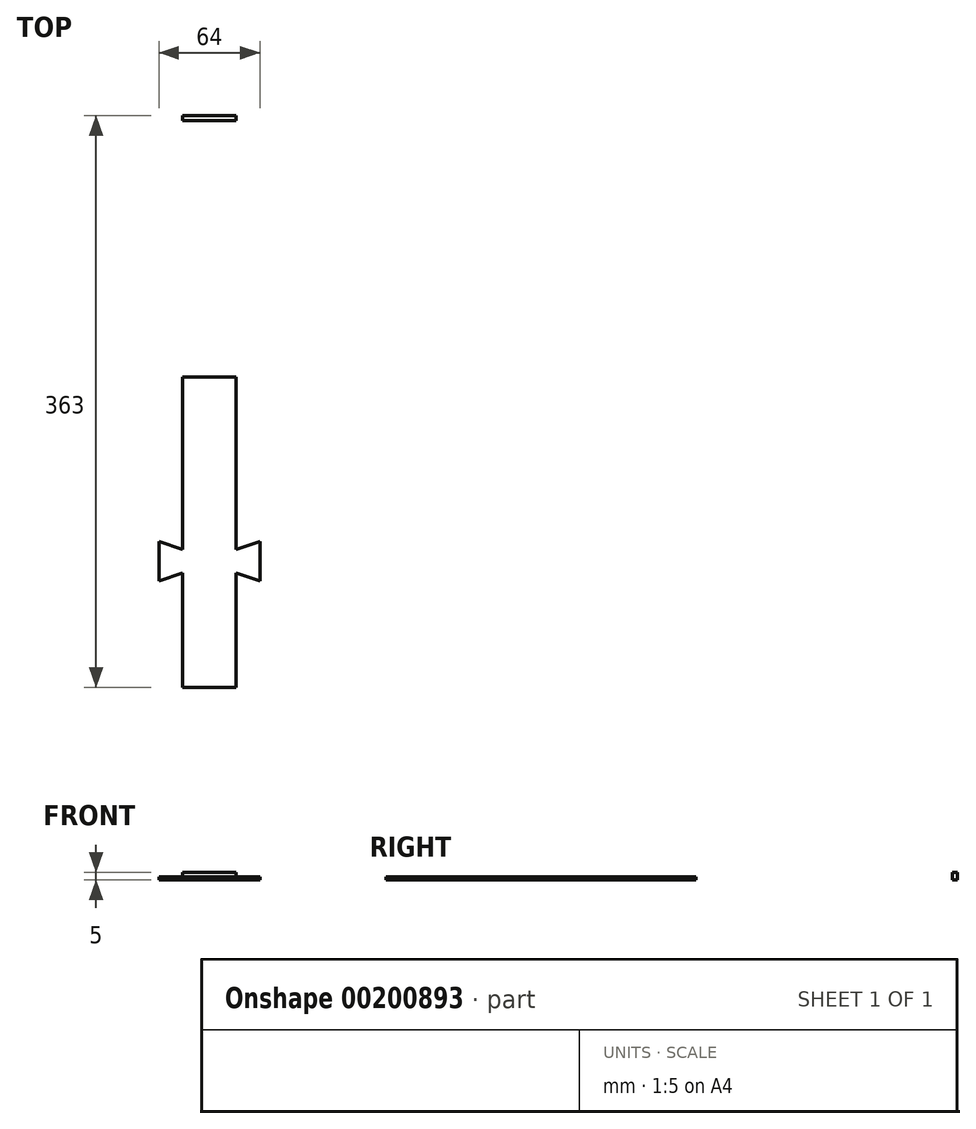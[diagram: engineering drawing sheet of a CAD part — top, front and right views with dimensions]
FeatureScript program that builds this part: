
annotation { "Feature Type Name" : "Feature", "Feature Type Description" : "" }
export const myFeature = defineFeature(function(context is Context, id is Id, definition is map)
    precondition{}
    {
        {
            var Q0;
            Q0=qCreatedBy(makeId("Top.planeOp"),FACE);
            var sketch = newSketch(context, id + "F0", { "sketchPlane" : qUnion([Q0])});
            skLineSegment(sketch, "E0.bottom", {"start": v(180, 180) * mm, "end": v(-180, 180) * mm});
            skLineSegment(sketch, "E0.top", {"start": v(180, -180) * mm, "end": v(-180, -180) * mm});
            skLineSegment(sketch, "E0.left", {"start": v(180, 180) * mm, "end": v(180, -180) * mm});
            skLineSegment(sketch, "E0.right", {"start": v(-180, 180) * mm, "end": v(-180, -180) * mm});
            skPoint(sketch, "E0.middle", {"position": v(0, 0) * mm});
            skLineSegment(sketch, "E1.bottom", {"start": v(183, 183) * mm, "end": v(-183, 183) * mm});
            skLineSegment(sketch, "E1.top", {"start": v(183, -183) * mm, "end": v(-183, -183) * mm});
            skLineSegment(sketch, "E1.left", {"start": v(183, 183) * mm, "end": v(183, -183) * mm});
            skLineSegment(sketch, "E1.right", {"start": v(-183, 183) * mm, "end": v(-183, -183) * mm});
            skSolve(sketch);
        }
        {
            var Q0;
            Q0=makeQuery(id+"F0.imprint","IMPRINT",FACE,{"disambiguationData":[TD([[makeQuery(id+"F0.imprint","IMPRINT",EDGE,{"derivedFrom":sQuery(id+"F0.wireOp",EDGE,"E0.bottom")}),1.0]])]});
            extrude(context, id + "F1", {"entities" : qUnion([Q0]), "depth" : 2 * mm});
        }
        {
            var Q0;
            Q0=makeQuery(id+"F0.imprint","IMPRINT",FACE,{"disambiguationData":[TD([[makeQuery(id+"F0.imprint","IMPRINT",EDGE,{"derivedFrom":sQuery(id+"F0.wireOp",EDGE,"E0.bottom")}),-1.0]])]});
            extrude(context, id + "F2", {"entities" : qUnion([Q0]), "operationType" : NewBodyOperationType.ADD, "depth" : 5 * mm});
        }
        {
            var Q0;
            Q0=makeQuery(id+"F2.opExtrude","CAP_FACE",FACE,{"disambiguationData":[OSD([sQuery(id+"F0.wireOp",EDGE,"E0.bottom"),sQuery(id+"F0.wireOp",EDGE,"E0.top"),sQuery(id+"F0.wireOp",EDGE,"E0.left"),sQuery(id+"F0.wireOp",EDGE,"E0.right"),sQuery(id+"F0.wireOp",EDGE,"E1.bottom"),sQuery(id+"F0.wireOp",EDGE,"E1.top"),sQuery(id+"F0.wireOp",EDGE,"E1.left"),sQuery(id+"F0.wireOp",EDGE,"E1.right")])],"isStart":false});
            var sketch = newSketch(context, id + "F3", { "sketchPlane" : qUnion([Q0])});
            skLineSegment(sketch, "E2", {"start": v(0, 0) * mm, "end": v(0, 194.54) * mm, "construction": true});
            skPoint(sketch, "E2.endSnap0", {"position": v(0, 183) * mm});
            skLineSegment(sketch, "E3", {"start": v(0, 194.54) * mm, "end": v(0, 0) * mm, "construction": true});
            skLineSegment(sketch, "E4", {"start": v(220.84, 0) * mm, "end": v(0, 0) * mm, "construction": true});
            skLineSegment(sketch, "E5.bottom", {"start": v(17, -17) * mm, "end": v(-92.5, -17) * mm});
            skLineSegment(sketch, "E5.top", {"start": v(17, 183) * mm, "end": v(-183, 183) * mm});
            skLineSegment(sketch, "E5.left", {"start": v(17, -17) * mm, "end": v(17, 92.5) * mm});
            skLineSegment(sketch, "E5.right", {"start": v(-183, -17) * mm, "end": v(-183, 183) * mm});
            skPoint(sketch, "E5.middle", {"position": v(-83, 83) * mm});
            skLineSegment(sketch, "E6.MirrorCS", {"start": v(-17, -17) * mm, "end": v(-17, 92.5) * mm});
            skLineSegment(sketch, "E7.MirrorCS", {"start": v(17, 17) * mm, "end": v(-92.5, 17) * mm});
            skLineSegment(sketch, "E8", {"start": v(-17, 17) * mm, "end": v(-17, 92.5) * mm, "construction": true});
            skLineSegment(sketch, "E9", {"start": v(-17, 100) * mm, "end": v(-183, 100) * mm, "construction": true});
            skLineSegment(sketch, "E10", {"start": v(-100, 17) * mm, "end": v(-100, 183) * mm, "construction": true});
            skLineSegment(sketch, "E11", {"start": v(-32, 87.5) * mm, "end": v(-32, 112.5) * mm});
            skLineSegment(sketch, "E12", {"start": v(-17, 92.5) * mm, "end": v(-32, 87.5) * mm});
            skLineSegment(sketch, "E13.MirrorCS", {"start": v(-17, 107.5) * mm, "end": v(-32, 112.5) * mm});
            skLineSegment(sketch, "E14.MirrorCS", {"start": v(17, 92.5) * mm, "end": v(32, 87.5) * mm});
            skLineSegment(sketch, "E15.MirrorCS", {"start": v(32, 87.5) * mm, "end": v(32, 112.5) * mm});
            skLineSegment(sketch, "E16.MirrorCS", {"start": v(17, 107.5) * mm, "end": v(32, 112.5) * mm});
            skLineSegment(sketch, "E17.trimOffspring", {"start": v(17, 107.5) * mm, "end": v(17, 183) * mm});
            skLineSegment(sketch, "E18.trimOffspring", {"start": v(-17, 107.5) * mm, "end": v(-17, 183) * mm, "construction": true});
            skLineSegment(sketch, "E19.trimOffspring", {"start": v(-17, 107.5) * mm, "end": v(-17, 183) * mm});
            skLineSegment(sketch, "E20.1.0", {"start": v(17, 17) * mm, "end": v(92.5, 17) * mm, "construction": true});
            skLineSegment(sketch, "E20.1.2", {"start": v(17, 17) * mm, "end": v(17, 92.5) * mm, "construction": true});
            skLineSegment(sketch, "E20.1.5", {"start": v(107.5, 17) * mm, "end": v(112.5, 32) * mm});
            skPoint(sketch, "E20.1.6", {"position": v(83, 83) * mm});
            skLineSegment(sketch, "E20.1.7", {"start": v(-17, 17) * mm, "end": v(92.5, 17) * mm});
            skLineSegment(sketch, "E20.1.8", {"start": v(107.5, -17) * mm, "end": v(112.5, -32) * mm});
            skLineSegment(sketch, "E20.1.9", {"start": v(92.5, -17) * mm, "end": v(87.5, -32) * mm});
            skLineSegment(sketch, "E20.1.10", {"start": v(87.5, -32) * mm, "end": v(112.5, -32) * mm});
            skLineSegment(sketch, "E20.1.11", {"start": v(107.5, 17) * mm, "end": v(183, 17) * mm, "construction": true});
            skLineSegment(sketch, "E20.1.12", {"start": v(92.5, 17) * mm, "end": v(87.5, 32) * mm});
            skLineSegment(sketch, "E20.1.13", {"start": v(-17, -17) * mm, "end": v(92.5, -17) * mm});
            skLineSegment(sketch, "E20.1.14", {"start": v(87.5, 32) * mm, "end": v(112.5, 32) * mm});
            skLineSegment(sketch, "E20.1.16", {"start": v(107.5, -17) * mm, "end": v(183, -17) * mm});
            skLineSegment(sketch, "E20.1.18", {"start": v(107.5, 17) * mm, "end": v(183, 17) * mm});
            skLineSegment(sketch, "E20.2.0", {"start": v(17, -17) * mm, "end": v(17, -92.5) * mm, "construction": true});
            skLineSegment(sketch, "E20.2.5", {"start": v(17, -107.5) * mm, "end": v(32, -112.5) * mm});
            skPoint(sketch, "E20.2.6", {"position": v(83, -83) * mm});
            skLineSegment(sketch, "E20.2.7", {"start": v(17, 17) * mm, "end": v(17, -92.5) * mm});
            skLineSegment(sketch, "E20.2.8", {"start": v(-17, -107.5) * mm, "end": v(-32, -112.5) * mm});
            skLineSegment(sketch, "E20.2.9", {"start": v(-17, -92.5) * mm, "end": v(-32, -87.5) * mm});
            skLineSegment(sketch, "E20.2.10", {"start": v(-32, -87.5) * mm, "end": v(-32, -112.5) * mm});
            skLineSegment(sketch, "E20.2.11", {"start": v(17, -107.5) * mm, "end": v(17, -183) * mm, "construction": true});
            skLineSegment(sketch, "E20.2.12", {"start": v(17, -92.5) * mm, "end": v(32, -87.5) * mm});
            skLineSegment(sketch, "E20.2.13", {"start": v(-17, 17) * mm, "end": v(-17, -92.5) * mm});
            skLineSegment(sketch, "E20.2.14", {"start": v(32, -87.5) * mm, "end": v(32, -112.5) * mm});
            skLineSegment(sketch, "E20.2.15", {"start": v(-17, -17) * mm, "end": v(92.5, -17) * mm});
            skLineSegment(sketch, "E20.2.16", {"start": v(-17, -107.5) * mm, "end": v(-17, -183) * mm});
            skLineSegment(sketch, "E20.2.18", {"start": v(17, -107.5) * mm, "end": v(17, -183) * mm});
            skPoint(sketch, "E20.center", {"position": v(0, 0) * mm});
            skLineSegment(sketch, "E21.trimOffspring", {"start": v(107.5, -17) * mm, "end": v(183, -17) * mm, "construction": true});
            skLineSegment(sketch, "E22.trimOffspring", {"start": v(17, 107.5) * mm, "end": v(17, 183) * mm, "construction": true});
            skLineSegment(sketch, "E23.MirrorCS", {"start": v(-107.5, 17) * mm, "end": v(-112.5, 32) * mm});
            skLineSegment(sketch, "E24.MirrorCS", {"start": v(-87.5, 32) * mm, "end": v(-112.5, 32) * mm});
            skLineSegment(sketch, "E25.MirrorCS", {"start": v(-92.5, 17) * mm, "end": v(-87.5, 32) * mm});
            skLineSegment(sketch, "E26.MirrorCS", {"start": v(-92.5, -17) * mm, "end": v(-87.5, -32) * mm});
            skLineSegment(sketch, "E27.MirrorCS", {"start": v(-87.5, -32) * mm, "end": v(-112.5, -32) * mm});
            skLineSegment(sketch, "E28.MirrorCS", {"start": v(-107.5, -17) * mm, "end": v(-112.5, -32) * mm});
            skLineSegment(sketch, "E29.trimOffspring", {"start": v(-107.5, -17) * mm, "end": v(-183, -17) * mm});
            skLineSegment(sketch, "E30.trimOffspring", {"start": v(-100, 17) * mm, "end": v(-183, 17) * mm, "construction": true});
            skLineSegment(sketch, "E31.trimOffspring", {"start": v(-100, 17) * mm, "end": v(-183, 17) * mm});
            skLineSegment(sketch, "E32", {"start": v(-183, -17) * mm, "end": v(17, -17) * mm, "construction": true});
            skSolve(sketch);
        }
        {
            var Q0;
            {var subQ1=sQuery(id+"F3.wireOp",EDGE,"E5.top");var subQ3=sQuery(id+"F3.wireOp",EDGE,"E19.trimOffspring");var subQ4=makeQuery(id+"F3.imprint","INTERSECT",VERTEX,{"derivedFrom":[subQ1,subQ3]});Q0=makeQuery(id+"F3.imprint","IMPRINT",FACE,{"disambiguationData":[TD([[makeQuery(id+"F3.imprint","IMPRINT",EDGE,{"disambiguationData":[TD([[subQ4,1.0]])],"derivedFrom":subQ3}),-1.0]])]});}
            var Q1;
            {var subQ2=sQuery(id+"F3.wireOp",EDGE,"E6.MirrorCS");Q1=makeQuery(id+"F3.imprint","IMPRINT",FACE,{"disambiguationData":[TD([[makeQuery(id+"F3.imprint","IMPRINT",EDGE,{"derivedFrom":subQ2}),-1.0]])]});}
            var Q2;
            {var subQ3=sQuery(id+"F3.wireOp",EDGE,"E20.2.7");var subQ5=sQuery(id+"F3.wireOp",EDGE,"E20.2.15");var subQ6=makeQuery(id+"F3.imprint","INTERSECT",VERTEX,{"derivedFrom":[subQ3,subQ5]});Q2=makeQuery(id+"F3.imprint","IMPRINT",FACE,{"disambiguationData":[TD([[makeQuery(id+"F3.imprint","IMPRINT",EDGE,{"disambiguationData":[TD([[subQ6,1.0]])],"derivedFrom":subQ3}),-1.0]])]});}
            extrude(context, id + "F4", {"entities" : qUnion([Q0, Q1, Q2]), "operationType" : NewBodyOperationType.INTERSECT, "endBound" : BoundingType.SYMMETRIC, "depth" : 25 * mm});
        }
    });
